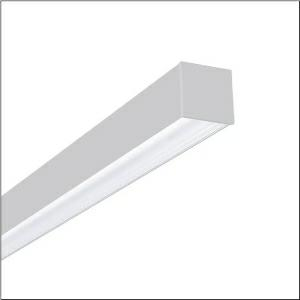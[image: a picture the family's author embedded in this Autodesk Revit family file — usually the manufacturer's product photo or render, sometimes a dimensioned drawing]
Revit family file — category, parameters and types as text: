
# Revit family: silica_r_5mx21bd2w4a_b787
name_source: partatom
category: Lighting Fixtures
units: mm (PartAtom-declared; Revit-internal decimal feet)

## family parameters
Cut with Voids When Loaded = No
Host = Face
Light Source = No
Part Type = Normal
Room Calculation Point = No
Round Connector Dimension = Use Diameter
Shared = No

## types (1)
- --- (1 x LED, 9910 lm, 60.1 W, 4000K)
    Apparent Load = 60 VA
    CIE Flux Codes = 82 97 100 100 100
    Color Rendering = 80
    Color Temperature = 4000K
    Default Elevation = 1800 mm
    Description = Silica®, office luminaire, of aluminium, light emission: direct distribution, primary light characteristic: symmetric, installation type: surface-mounted, LED rated luminous flux: 9.910 lm, light colour: 840, colour temperature: 4000K, control gear: ECG DALI, with terminal, 3+2-pole, max. 2.5mm², mains connection: 230V, AC, 50/60Hz, rated input power: 60W, luminaire housing, of aluminium, traffic white (RAL 9016), length: 2.880 mm, width: 64 mm, height: 64mm, protection rating (complete): IP20, insulation class (complete): insulation class I (protective earthing), certification: CE, permissible ambient temperature for indoor applications: 0..+35°C, standard: EN 50419, packaging unit: 1 piece
    Height = 64 mm
    Lamp = 1 x LED
    Lamp Light Flux = 9910 lm
    Lamp Power = 60.1 W
    Lamp count = 1
    Length = 2845 mm
    Luminous efficacy = 165 lm/W
    Manufacturer = Siteco
    ModVariant = No
    Model = 5MX21BD2W4A
    Mounting Place = Ceiling
    Mounting Type = Surface mounted
    Number of Poles = 1
    OnlyDefault = Yes
    Power Factor = 1
    Product Name = Silica®
    Product group = office luminaire | ceiling mounted
    ProductGroupID = 302
    Protection Class = Protection class I
    Protection Degree = IP 20
    RLX_Detail_Level = 1
    RlxData = <blob elided: 23337 chars, md5=7da22011>
    Socket = socket
    Standby Power = 0 W
    System Light Flux = 9910 lm
    System Power = 60 W
    Type Comments = factory setting: luminous flux: 100 % | dim-lin: 254 | 336 mA
    Type Image = l_1003937.jpg
    URL = http://relux.com
    VarID = @adj_132190
    Voltage = 0 V
    Weight = 0.00 kg
    Width = 66 mm

## geometry (parser evidence)
native form markers: Blend x4, Sweep x10
no freeform markers — native parametric forms only
